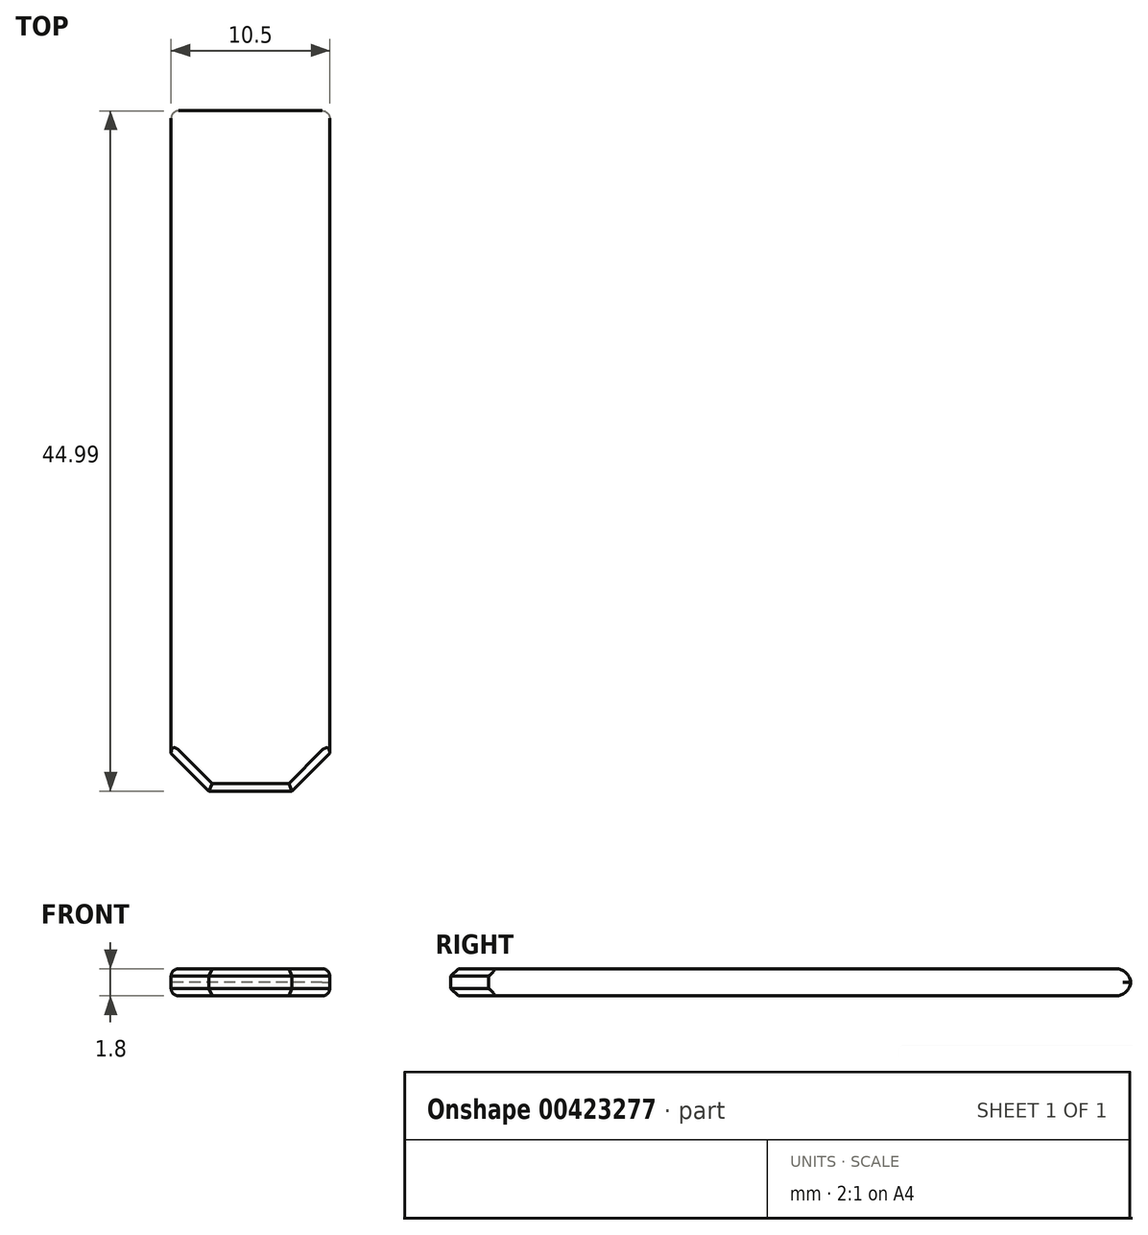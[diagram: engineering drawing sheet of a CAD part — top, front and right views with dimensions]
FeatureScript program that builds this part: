
annotation { "Feature Type Name" : "Feature", "Feature Type Description" : "" }
export const myFeature = defineFeature(function(context is Context, id is Id, definition is map)
    precondition{}
    {
        {
            var Q0;
            Q0=qCreatedBy(makeId("Top.planeOp"),FACE);
            var sketch = newSketch(context, id + "F0", { "sketchPlane" : qUnion([Q0])});
            skLineSegment(sketch, "E0.bottom", {"start": v(5.25, -22.5) * mm, "end": v(-5.25, -22.5) * mm});
            skLineSegment(sketch, "E0.left", {"start": v(5.25, -22.5) * mm, "end": v(5.25, 22.5) * mm});
            skLineSegment(sketch, "E0.right", {"start": v(-5.25, -22.5) * mm, "end": v(-5.25, 22.5) * mm});
            skPoint(sketch, "E0.middle", {"position": v(0, 0) * mm});
            skLineSegment(sketch, "E1", {"start": v(-5.25, 22.5) * mm, "end": v(5.25, 22.5) * mm});
            skSolve(sketch);
        }
        {
            var Q0;
            Q0=qSketchRegion(id+"F0",true);
            extrude(context, id + "F1", {"entities" : qUnion([Q0]), "depth" : 1.8 * mm});
        }
        {
            var Q0;
            Q0=makeQuery(id+"F1.opExtrude","SWEPT_EDGE",EDGE,{"disambiguationData":[OSD([sQuery(id+"F0.wireOp",EDGE,"E0.bottom"),sQuery(id+"F0.wireOp",EDGE,"E0.left")])]});
            var Q1;
            Q1=makeQuery(id+"F1.opExtrude","SWEPT_EDGE",EDGE,{"disambiguationData":[OSD([sQuery(id+"F0.wireOp",EDGE,"E0.bottom"),sQuery(id+"F0.wireOp",EDGE,"E0.right")])]});
            chamfer(context, id + "F2", {"entities" : qUnion([Q0, Q1]), "width" : 2.5 * mm, "tangentPropagation" : true});
        }
        {
            var Q0;
            Q0=makeQuery(id+"F1.opExtrude","CAP_EDGE",EDGE,{"disambiguationData":[OSD([sQuery(id+"F0.wireOp",EDGE,"E0.bottom")])],"isStart":false});
            var Q1;
            {var subQ0=sQuery(id+"F0.wireOp",EDGE,"E0.left");var subQ1=sQuery(id+"F0.wireOp",EDGE,"E0.bottom");Q1=makeQuery(id+"F2.opChamfer","BLEND_EDGE",EDGE,{"blendedFrom":[makeQuery(id+"F1.opExtrude","SWEPT_EDGE",EDGE,{"disambiguationData":[OSD([subQ1,subQ0])]}),makeQuery(id+"F1.opExtrude","CAP_FACE",FACE,{"disambiguationData":[OSD([subQ1,subQ0,sQuery(id+"F0.wireOp",EDGE,"E0.right"),sQuery(id+"F0.wireOp",EDGE,"E1")])],"isStart":false})],"blendedInto":[makeQuery(id+"F1.opExtrude","CAP_FACE",FACE,{"disambiguationData":[OSD([subQ1,subQ0,sQuery(id+"F0.wireOp",EDGE,"E0.right"),sQuery(id+"F0.wireOp",EDGE,"E1")])],"isStart":false})]});}
            var Q2;
            {var subQ0=sQuery(id+"F0.wireOp",EDGE,"E0.left");var subQ1=sQuery(id+"F0.wireOp",EDGE,"E0.bottom");Q2=makeQuery(id+"F2.opChamfer","BLEND_EDGE",EDGE,{"blendedFrom":[makeQuery(id+"F1.opExtrude","SWEPT_EDGE",EDGE,{"disambiguationData":[OSD([subQ1,subQ0])]}),makeQuery(id+"F1.opExtrude","CAP_FACE",FACE,{"disambiguationData":[OSD([subQ1,subQ0,sQuery(id+"F0.wireOp",EDGE,"E0.right"),sQuery(id+"F0.wireOp",EDGE,"E1")])],"isStart":true})],"blendedInto":[makeQuery(id+"F1.opExtrude","CAP_FACE",FACE,{"disambiguationData":[OSD([subQ1,subQ0,sQuery(id+"F0.wireOp",EDGE,"E0.right"),sQuery(id+"F0.wireOp",EDGE,"E1")])],"isStart":true})]});}
            var Q3;
            Q3=makeQuery(id+"F1.opExtrude","CAP_EDGE",EDGE,{"disambiguationData":[OSD([sQuery(id+"F0.wireOp",EDGE,"E0.bottom")])],"isStart":true});
            var Q4;
            {var subQ0=sQuery(id+"F0.wireOp",EDGE,"E0.right");var subQ1=sQuery(id+"F0.wireOp",EDGE,"E0.bottom");Q4=makeQuery(id+"F2.opChamfer","BLEND_EDGE",EDGE,{"blendedFrom":[makeQuery(id+"F1.opExtrude","SWEPT_EDGE",EDGE,{"disambiguationData":[OSD([subQ1,subQ0])]}),makeQuery(id+"F1.opExtrude","CAP_FACE",FACE,{"disambiguationData":[OSD([subQ1,sQuery(id+"F0.wireOp",EDGE,"E0.left"),subQ0,sQuery(id+"F0.wireOp",EDGE,"E1")])],"isStart":false})],"blendedInto":[makeQuery(id+"F1.opExtrude","CAP_FACE",FACE,{"disambiguationData":[OSD([subQ1,sQuery(id+"F0.wireOp",EDGE,"E0.left"),subQ0,sQuery(id+"F0.wireOp",EDGE,"E1")])],"isStart":false})]});}
            var Q5;
            {var subQ0=sQuery(id+"F0.wireOp",EDGE,"E0.right");var subQ1=sQuery(id+"F0.wireOp",EDGE,"E0.bottom");Q5=makeQuery(id+"F2.opChamfer","BLEND_EDGE",EDGE,{"blendedFrom":[makeQuery(id+"F1.opExtrude","SWEPT_EDGE",EDGE,{"disambiguationData":[OSD([subQ1,subQ0])]}),makeQuery(id+"F1.opExtrude","CAP_FACE",FACE,{"disambiguationData":[OSD([subQ1,sQuery(id+"F0.wireOp",EDGE,"E0.left"),subQ0,sQuery(id+"F0.wireOp",EDGE,"E1")])],"isStart":true})],"blendedInto":[makeQuery(id+"F1.opExtrude","CAP_FACE",FACE,{"disambiguationData":[OSD([subQ1,sQuery(id+"F0.wireOp",EDGE,"E0.left"),subQ0,sQuery(id+"F0.wireOp",EDGE,"E1")])],"isStart":true})]});}
            chamfer(context, id + "F3", {"entities" : qUnion([Q0, Q1, Q2, Q3, Q4, Q5]), "width" : 0.5 * mm, "tangentPropagation" : true});
        }
        {
            var Q0;
            Q0=makeQuery(id+"F1.opExtrude","CAP_EDGE",EDGE,{"disambiguationData":[OSD([sQuery(id+"F0.wireOp",EDGE,"E1")])],"isStart":true});
            var Q1;
            Q1=makeQuery(id+"F1.opExtrude","CAP_EDGE",EDGE,{"disambiguationData":[OSD([sQuery(id+"F0.wireOp",EDGE,"E1")])],"isStart":false});
            fillet(context, id + "F4", {"entities" : qUnion([Q0, Q1]), "radius" : 1 * mm, "tangentPropagation" : true, "allowEdgeOverflow" : false});
        }
        {
            var Q0;
            Q0=makeQuery(id+"F1.opExtrude","CAP_EDGE",EDGE,{"disambiguationData":[OSD([sQuery(id+"F0.wireOp",EDGE,"E0.left")])],"isStart":false});
            var Q1;
            Q1=makeQuery(id+"F1.opExtrude","CAP_EDGE",EDGE,{"disambiguationData":[OSD([sQuery(id+"F0.wireOp",EDGE,"E0.left")])],"isStart":true});
            var Q2;
            Q2=makeQuery(id+"F1.opExtrude","CAP_EDGE",EDGE,{"disambiguationData":[OSD([sQuery(id+"F0.wireOp",EDGE,"E0.right")])],"isStart":false});
            var Q3;
            Q3=makeQuery(id+"F1.opExtrude","CAP_EDGE",EDGE,{"disambiguationData":[OSD([sQuery(id+"F0.wireOp",EDGE,"E0.right")])],"isStart":true});
            fillet(context, id + "F5", {"entities" : qUnion([Q0, Q1, Q2, Q3]), "radius" : 0.5 * mm, "tangentPropagation" : true, "allowEdgeOverflow" : false});
        }
    });
